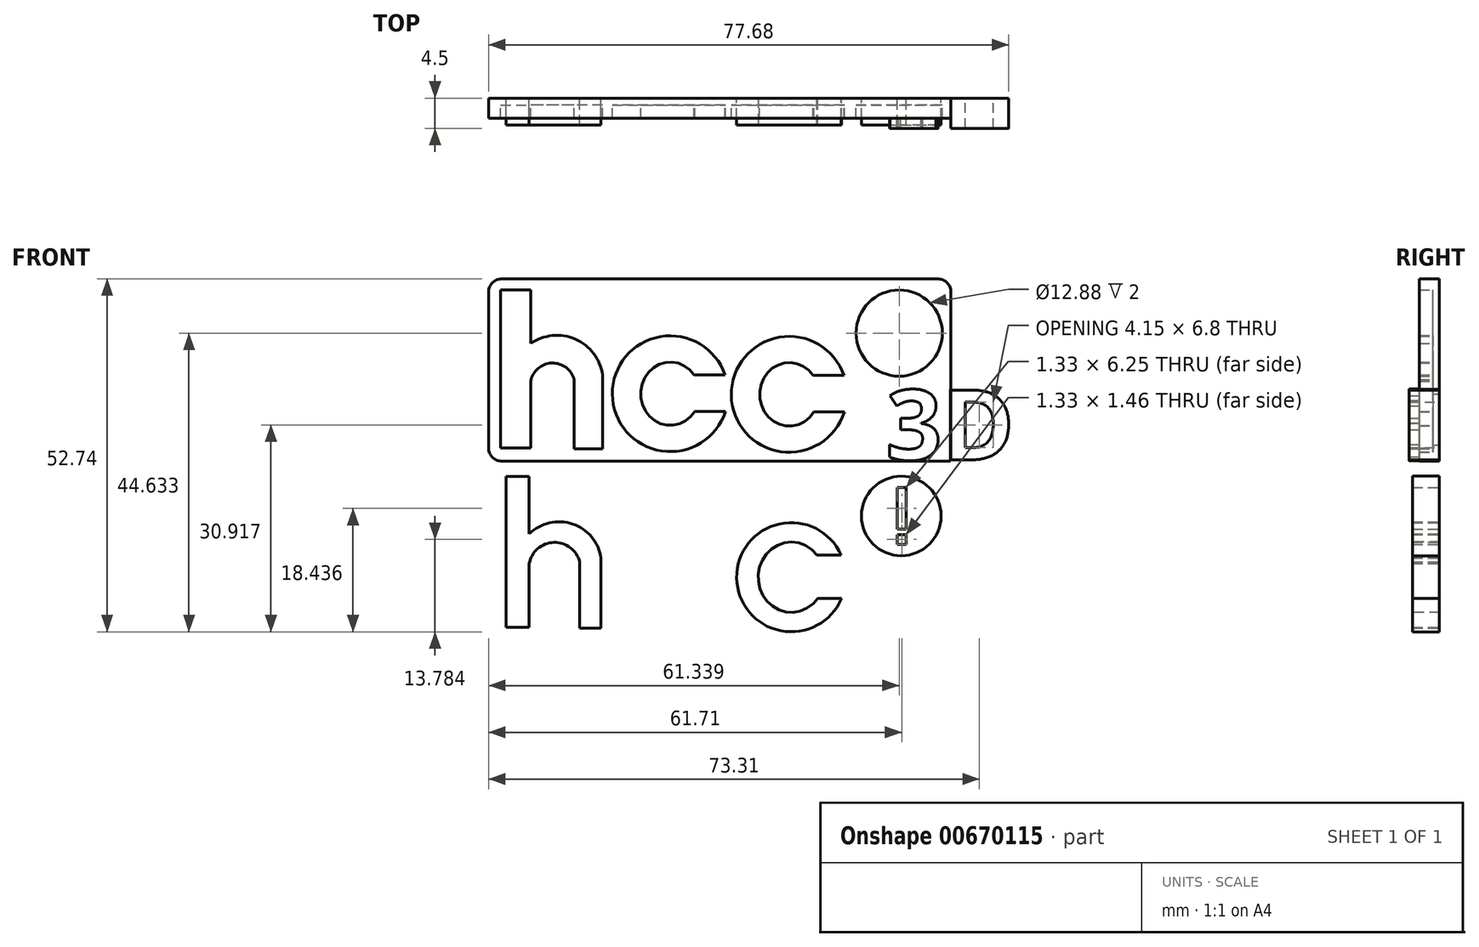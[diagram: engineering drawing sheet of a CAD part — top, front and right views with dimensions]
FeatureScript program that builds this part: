
annotation { "Feature Type Name" : "Feature", "Feature Type Description" : "" }
export const myFeature = defineFeature(function(context is Context, id is Id, definition is map)
    precondition{}
    {
        {
            var Q0;
            Q0=qCreatedBy(makeId("Front.planeOp"),FACE);
            var sketch = newSketch(context, id + "F0", { "sketchPlane" : qUnion([Q0])});
            skLineSegment(sketch, "E0.bottom", {"start": v(32.84, -11.61) * mm, "end": v(-34.55, -11.61) * mm});
            skLineSegment(sketch, "E0.top", {"start": v(32.84, 13.5) * mm, "end": v(-34.55, 13.5) * mm});
            skLineSegment(sketch, "E0.left", {"start": v(32.84, -11.61) * mm, "end": v(32.84, 13.5) * mm});
            skLineSegment(sketch, "E0.right", {"start": v(-34.55, -11.61) * mm, "end": v(-34.55, 13.5) * mm});
            skLineSegment(sketch, "E1.bottom", {"start": v(32.84, -2.93) * mm, "end": v(35.45, -2.93) * mm});
            skLineSegment(sketch, "E1.top", {"start": v(32.84, -10.58) * mm, "end": v(35.45, -10.58) * mm});
            skLineSegment(sketch, "E1.left", {"start": v(32.84, -2.93) * mm, "end": v(32.84, -10.58) * mm});
            skLineSegment(sketch, "E1.right", {"start": v(35.45, -2.93) * mm, "end": v(35.45, -10.58) * mm});
            skSolve(sketch);
        }
        {
            var Q0;
            Q0=qCreatedBy(makeId("Front.planeOp"),FACE);
            var sketch = newSketch(context, id + "F1", { "sketchPlane" : qUnion([Q0])});
            skLineSegment(sketch, "E2.bottom", {"start": v(-29.23, 12.7) * mm, "end": v(-33.71, 12.7) * mm});
            skLineSegment(sketch, "E2.top", {"start": v(-29.23, -10.95) * mm, "end": v(-33.71, -10.95) * mm});
            skLineSegment(sketch, "E2.left", {"start": v(-29.23, 12.7) * mm, "end": v(-29.23, 4.68) * mm});
            skLineSegment(sketch, "E2.right", {"start": v(-33.71, 12.7) * mm, "end": v(-33.71, -10.95) * mm});
            skArc(sketch, "E3", {"start": v(-18.5, 0) * mm, "mid": v(-22.56, 5.32) * mm, "end": v(-29.23, 4.68) * mm});
            skArc(sketch, "E4", {"start": v(-22.75, -0.72) * mm, "mid": v(-26.08, 1.76) * mm, "end": v(-29.23, -0.94) * mm});
            skLineSegment(sketch, "E5", {"start": v(-22.75, -0.72) * mm, "end": v(-22.75, -11.06) * mm});
            skLineSegment(sketch, "E6", {"start": v(-22.75, -11.06) * mm, "end": v(-18.5, -11.06) * mm});
            skLineSegment(sketch, "E7", {"start": v(-18.5, -11.06) * mm, "end": v(-18.5, 0) * mm});
            skArc(sketch, "E8", {"start": v(-0.2, 0) * mm, "mid": v(-17.04, -2.91) * mm, "end": v(-0.14, -5.47) * mm});
            skEllipticalArc(sketch, "E9", {});
            skLineSegment(sketch, "E10", {"start": v(-4.83, 0) * mm, "end": v(0, 0) * mm});
            skLineSegment(sketch, "E11", {"start": v(-4.72, -5.47) * mm, "end": v(0, -5.47) * mm});
            skArc(sketch, "E12", {"start": v(17.56, -0.1) * mm, "mid": v(0.73, -3) * mm, "end": v(17.62, -5.56) * mm});
            skEllipticalArc(sketch, "E13", {});
            skLineSegment(sketch, "E14", {"start": v(12.93, -0.1) * mm, "end": v(17.76, -0.1) * mm});
            skLineSegment(sketch, "E15", {"start": v(13.05, -5.56) * mm, "end": v(17.76, -5.56) * mm});
            skCircle(sketch, "E16", {"center": v(25.8, 6.23) * mm, "radius": 6.44 * mm});
            skLineSegment(sketch, "E17.bottom", {"start": v(25.21, 10.49) * mm, "end": v(26.54, 10.49) * mm});
            skLineSegment(sketch, "E17.top", {"start": v(25.21, 4.24) * mm, "end": v(26.54, 4.24) * mm});
            skLineSegment(sketch, "E17.left", {"start": v(25.21, 10.49) * mm, "end": v(25.21, 4.24) * mm});
            skLineSegment(sketch, "E17.right", {"start": v(26.54, 10.49) * mm, "end": v(26.54, 4.24) * mm});
            skLineSegment(sketch, "E18.bottom", {"start": v(25.21, 3.44) * mm, "end": v(26.54, 3.44) * mm});
            skLineSegment(sketch, "E18.top", {"start": v(25.21, 1.98) * mm, "end": v(26.54, 1.98) * mm});
            skLineSegment(sketch, "E18.left", {"start": v(25.21, 3.44) * mm, "end": v(25.21, 1.98) * mm});
            skLineSegment(sketch, "E18.right", {"start": v(26.54, 3.44) * mm, "end": v(26.54, 1.98) * mm});
            skLineSegment(sketch, "E19.bottom", {"start": v(-35.53, 14.34) * mm, "end": v(33.55, 14.34) * mm});
            skLineSegment(sketch, "E19.top", {"start": v(-35.53, -12.91) * mm, "end": v(33.55, -12.91) * mm});
            skLineSegment(sketch, "E19.left", {"start": v(-35.53, 14.34) * mm, "end": v(-35.53, -12.91) * mm});
            skLineSegment(sketch, "E19.right", {"start": v(33.55, 14.34) * mm, "end": v(33.55, -12.91) * mm});
            skPoint(sketch, "E20.orphan", {"position": v(-32.13, 0) * mm});
            skLineSegment(sketch, "E21.trimOffspring", {"start": v(-29.23, -0.94) * mm, "end": v(-29.23, -10.95) * mm});
            skText(sketch, "E22", { "text": "3D", "fontName": "OpenSans-Bold.ttf"});
            skLineSegment(sketch, "E23.bottom", {"start": v(33.46, -2.18) * mm, "end": v(33.55, -2.18) * mm});
            skLineSegment(sketch, "E23.top", {"start": v(33.46, -2.18) * mm, "end": v(33.55, -2.18) * mm});
            skLineSegment(sketch, "E23.left", {"start": v(33.55, -2.18) * mm, "end": v(33.55, -2.18) * mm});
            skLineSegment(sketch, "E23.right", {"start": v(33.46, -2.18) * mm, "end": v(33.46, -2.18) * mm});
            skLineSegment(sketch, "E24.bottom", {"start": v(33.55, -12.71) * mm, "end": v(33.46, -12.71) * mm});
            skLineSegment(sketch, "E24.top", {"start": v(33.55, -12.91) * mm, "end": v(33.46, -12.91) * mm});
            skLineSegment(sketch, "E24.left", {"start": v(33.46, -12.91) * mm, "end": v(33.46, -12.71) * mm});
            skLineSegment(sketch, "E24.right", {"start": v(33.55, -12.91) * mm, "end": v(33.55, -12.71) * mm});
            skLineSegment(sketch, "E25.bottom", {"start": v(33.64, -12.71) * mm, "end": v(33.46, -12.71) * mm});
            skLineSegment(sketch, "E25.top", {"start": v(33.55, -2.18) * mm, "end": v(33.46, -2.18) * mm});
            skLineSegment(sketch, "E25.left", {"start": v(33.46, -12.71) * mm, "end": v(33.46, -2.18) * mm});
            skLineSegment(sketch, "E26.top", {"start": v(33.46, -2.76) * mm, "end": v(33.55, -2.76) * mm});
            skLineSegment(sketch, "E26.left", {"start": v(33.55, -2.18) * mm, "end": v(33.55, -2.76) * mm});
            skLineSegment(sketch, "E26.right", {"start": v(33.46, -2.18) * mm, "end": v(33.46, -2.76) * mm});
            skLineSegment(sketch, "E27.left", {"start": v(33.55, -3.88) * mm, "end": v(33.55, -12.94) * mm});
            skPoint(sketch, "E28.end.orphan", {"position": v(36.71, 0) * mm});
            skPoint(sketch, "E28.start.orphan", {"position": v(33.55, 0) * mm});
            const initialGuessF1  = {"E9": [-0.00838379468768835, -0.002821371890604496, 0, 1, 0.004734611138701439, 0.0044216665190650265, 5.350779379737523, 4.11952951118792], "E13": [0.009380069561302662, -0.0029154655057936907, 0, 1, 0.004734611138701439, 0.0044216665190650265, 5.350779379737523, 4.11952951118792], "E22": [0.02383, -0.01271, 1, 0, 0.01053]};
            skSetInitialGuess(sketch, initialGuessF1);
            skSolve(sketch);
        }
        {
            var Q0;
            Q0=qSketchRegion(id+"F0",true);
            extrude(context, id + "F2", {"entities" : qUnion([Q0]), "depth" : 1 * mm, "offsetDistance" : 25 * mm});
        }
        {
            var Q0;
            Q0=qCreatedBy(makeId("Front.planeOp"),FACE);
            var sketch = newSketch(context, id + "F3", { "sketchPlane" : qUnion([Q0])});
            skLineSegment(sketch, "E29.bottom", {"start": v(-28.92, -14.64) * mm, "end": v(-33.4, -14.64) * mm});
            skLineSegment(sketch, "E29.top", {"start": v(-28.92, -38.27) * mm, "end": v(-33.4, -38.27) * mm});
            skLineSegment(sketch, "E29.left", {"start": v(-28.92, -14.64) * mm, "end": v(-28.92, -22.65) * mm});
            skLineSegment(sketch, "E29.right", {"start": v(-33.4, -14.64) * mm, "end": v(-33.4, -38.27) * mm});
            skArc(sketch, "E30", {"start": v(-18.2, -27.33) * mm, "mid": v(-22.26, -22) * mm, "end": v(-28.92, -22.65) * mm});
            skArc(sketch, "E31", {"start": v(-22.44, -28.05) * mm, "mid": v(-25.77, -25.57) * mm, "end": v(-28.92, -28.27) * mm});
            skLineSegment(sketch, "E32", {"start": v(-22.44, -28.05) * mm, "end": v(-22.44, -38.39) * mm});
            skLineSegment(sketch, "E33", {"start": v(-22.44, -38.39) * mm, "end": v(-18.2, -38.39) * mm});
            skLineSegment(sketch, "E34", {"start": v(-18.2, -38.39) * mm, "end": v(-18.2, -27.33) * mm});
            skArc(sketch, "E35", {"start": v(0.1, -27.32) * mm, "mid": v(-16.73, -30.25) * mm, "end": v(0.17, -32.77) * mm});
            skEllipticalArc(sketch, "E36", {});
            skLineSegment(sketch, "E37", {"start": v(-4.53, -27.33) * mm, "end": v(0.1, -27.32) * mm});
            skLineSegment(sketch, "E38", {"start": v(-4.4, -32.77) * mm, "end": v(0.16, -32.77) * mm});
            skArc(sketch, "E39", {"start": v(17.87, -27.42) * mm, "mid": v(1.03, -30.33) * mm, "end": v(17.93, -32.89) * mm});
            skEllipticalArc(sketch, "E40", {});
            skLineSegment(sketch, "E41", {"start": v(13.24, -27.42) * mm, "end": v(17.87, -27.42) * mm});
            skLineSegment(sketch, "E42", {"start": v(13.35, -32.89) * mm, "end": v(17.92, -32.89) * mm});
            skCircle(sketch, "E43", {"center": v(26.11, -21.1) * mm, "radius": 6.44 * mm});
            skLineSegment(sketch, "E44.bottom", {"start": v(25.52, -16.84) * mm, "end": v(26.84, -16.84) * mm});
            skLineSegment(sketch, "E44.top", {"start": v(25.52, -23.09) * mm, "end": v(26.84, -23.09) * mm});
            skLineSegment(sketch, "E44.left", {"start": v(25.52, -16.84) * mm, "end": v(25.52, -23.09) * mm});
            skLineSegment(sketch, "E44.right", {"start": v(26.84, -16.84) * mm, "end": v(26.84, -23.09) * mm});
            skLineSegment(sketch, "E45.bottom", {"start": v(25.52, -23.88) * mm, "end": v(26.84, -23.88) * mm});
            skLineSegment(sketch, "E45.top", {"start": v(25.52, -25.35) * mm, "end": v(26.84, -25.35) * mm});
            skLineSegment(sketch, "E45.left", {"start": v(25.52, -23.88) * mm, "end": v(25.52, -25.35) * mm});
            skLineSegment(sketch, "E45.right", {"start": v(26.84, -23.88) * mm, "end": v(26.84, -25.35) * mm});
            skPoint(sketch, "E46.orphan", {"position": v(-31.83, -27.33) * mm});
            skLineSegment(sketch, "E47.trimOffspring", {"start": v(-28.92, -28.27) * mm, "end": v(-28.92, -38.27) * mm});
            skLineSegment(sketch, "E48.0", {"start": v(-29.45, -15.16) * mm, "end": v(-29.45, -23.76) * mm});
            skArc(sketch, "E48.1", {"start": v(-18.72, -27.37) * mm, "mid": v(-22.99, -22.29) * mm, "end": v(-29.45, -23.76) * mm});
            skLineSegment(sketch, "E48.2", {"start": v(-29.45, -15.16) * mm, "end": v(-32.88, -15.16) * mm});
            skLineSegment(sketch, "E48.3", {"start": v(-18.72, -37.86) * mm, "end": v(-18.72, -27.37) * mm});
            skLineSegment(sketch, "E48.4", {"start": v(-21.91, -37.86) * mm, "end": v(-18.72, -37.86) * mm});
            skLineSegment(sketch, "E48.5", {"start": v(-21.91, -27.98) * mm, "end": v(-21.91, -37.86) * mm});
            skLineSegment(sketch, "E48.6", {"start": v(-32.88, -15.16) * mm, "end": v(-32.88, -37.75) * mm});
            skLineSegment(sketch, "E48.7", {"start": v(-29.45, -37.75) * mm, "end": v(-32.88, -37.75) * mm});
            skLineSegment(sketch, "E48.8", {"start": v(-29.45, -28.22) * mm, "end": v(-29.45, -37.75) * mm});
            skArc(sketch, "E48.9", {"start": v(-21.91, -27.98) * mm, "mid": v(-25.78, -25.04) * mm, "end": v(-29.45, -28.22) * mm});
            skCircle(sketch, "E49.0", {"center": v(26.11, -21.1) * mm, "radius": 5.94 * mm});
            skArc(sketch, "E50.0", {"start": v(-0.63, -26.82) * mm, "mid": v(-16.23, -30.26) * mm, "end": v(-0.55, -33.27) * mm});
            skLineSegment(sketch, "E50.1", {"start": v(-4.27, -26.83) * mm, "end": v(-0.63, -26.82) * mm});
            skFitSpline(sketch, "E50.2", {"points": [v(-7.1, -24.98) * mm, v(-8.08, -24.88) * mm, v(-9.05, -24.98) * mm, v(-9.98, -25.28) * mm, v(-10.85, -25.78) * mm, v(-11.6, -26.44) * mm, v(-12.2, -27.23) * mm, v(-12.66, -28.15) * mm, v(-12.94, -29.12) * mm, v(-13.03, -30.15) * mm, v(-12.94, -31.17) * mm, v(-12.66, -32.15) * mm, v(-12.2, -33.06) * mm, v(-11.6, -33.86) * mm, v(-10.85, -34.52) * mm, v(-9.98, -35.01) * mm, v(-9.05, -35.31) * mm, v(-8.08, -35.42) * mm, v(-7.1, -35.31) * mm, v(-6.17, -35.01) * mm, v(-5.31, -34.52) * mm, v(-4.56, -33.86) * mm, v(-3.95, -33.06) * mm, v(-3.5, -32.15) * mm, v(-3.22, -31.17) * mm, v(-3.13, -30.15) * mm, v(-3.22, -29.12) * mm, v(-3.5, -28.15) * mm, v(-3.95, -27.23) * mm, v(-4.56, -26.44) * mm, v(-5.31, -25.78) * mm, v(-6.17, -25.28) * mm, v(-7.1, -24.98) * mm, v(-8.08, -24.88) * mm, v(-9.05, -24.98) * mm]});
            skLineSegment(sketch, "E50.3", {"start": v(-4.13, -33.27) * mm, "end": v(-0.55, -33.27) * mm});
            skArc(sketch, "E51.0", {"start": v(17.13, -26.92) * mm, "mid": v(1.53, -30.34) * mm, "end": v(17.2, -33.39) * mm});
            skLineSegment(sketch, "E51.1", {"start": v(13.49, -26.92) * mm, "end": v(17.13, -26.92) * mm});
            skFitSpline(sketch, "E51.2", {"points": [v(13.65, -27.14) * mm, v(13.34, -26.7) * mm, v(12.78, -26.1) * mm, v(11.89, -25.53) * mm, v(11.16, -25.23) * mm, v(10.4, -25.04) * mm, v(9.6, -24.99) * mm, v(8.83, -25.06) * mm, v(8.07, -25.27) * mm, v(7.35, -25.6) * mm, v(6.7, -26.05) * mm, v(6.11, -26.6) * mm, v(5.62, -27.25) * mm, v(5.23, -27.96) * mm, v(4.95, -28.73) * mm, v(4.79, -29.54) * mm, v(4.74, -30.36) * mm, v(4.82, -31.18) * mm, v(5.02, -31.97) * mm, v(5.33, -32.73) * mm, v(5.75, -33.43) * mm, v(6.27, -34.04) * mm, v(6.88, -34.57) * mm, v(7.55, -34.98) * mm, v(8.28, -35.28) * mm, v(9.05, -35.46) * mm, v(9.83, -35.5) * mm, v(10.62, -35.4) * mm, v(11.37, -35.18) * mm, v(12.08, -34.84) * mm, v(12.95, -34.22) * mm, v(13.49, -33.61) * mm, v(13.77, -33.16) * mm]});
            skLineSegment(sketch, "E51.3", {"start": v(13.62, -33.39) * mm, "end": v(17.2, -33.39) * mm});
            const initialGuessF3  = {"E36": [-0.008079084567725658, -0.030148023739457127, 0, 1, 0.004734611138701439, 0.0044216665190650265, 5.350779407726535, 4.125229414550572], "E40": [0.009684779681265354, -0.03024211735464632, 0, 1, 0.004734611138701439, 0.0044216665190650265, 5.350779379737523, 4.11915715223877]};
            skSetInitialGuess(sketch, initialGuessF3);
            skSolve(sketch);
        }
        {
            var Q0;
            Q0=makeQuery(id+"F1.imprint","IMPRINT",FACE,{"disambiguationData":[TD([[makeQuery(id+"F1.imprint","IMPRINT",EDGE,{"derivedFrom":sQuery(id+"F1.wireOp",EDGE,"E22.sketch_text.stroke-27")}),-1.0]])]});
            var Q1;
            Q1=makeQuery(id+"F1.imprint","IMPRINT",FACE,{"disambiguationData":[TD([[makeQuery(id+"F1.imprint","IMPRINT",EDGE,{"derivedFrom":sQuery(id+"F1.wireOp",EDGE,"E22.sketch_text.stroke-0")}),-1.0]])]});
            extrude(context, id + "F4", {"entities" : qUnion([Q0, Q1]), "operationType" : NewBodyOperationType.ADD, "depth" : 4.5 * mm, "offsetDistance" : 25 * mm});
        }
        {
            var Q0;
            Q0=makeQuery(id+"F1.imprint","IMPRINT",FACE,{"disambiguationData":[TD([[makeQuery(id+"F1.imprint","IMPRINT",EDGE,{"derivedFrom":sQuery(id+"F1.wireOp",EDGE,"E22.sketch_text.stroke-27")}),-1.0]])]});
            var Q1;
            Q1=makeQuery(id+"F1.imprint","IMPRINT",FACE,{"disambiguationData":[TD([[makeQuery(id+"F1.imprint","IMPRINT",EDGE,{"derivedFrom":sQuery(id+"F1.wireOp",EDGE,"E2.bottom")}),-1.0]])]});
            extrude(context, id + "F5", {"entities" : qUnion([Q0, Q1]), "operationType" : NewBodyOperationType.ADD, "depth" : 3 * mm, "offsetDistance" : 25 * mm});
        }
        {
            var Q0;
            Q0=makeQuery(id+"F5.opExtrude","SWEPT_EDGE",EDGE,{"disambiguationData":[OSD([sQuery(id+"F1.wireOp",EDGE,"E19.bottom"),sQuery(id+"F1.wireOp",EDGE,"E19.left")])]});
            var Q1;
            Q1=makeQuery(id+"F5.opExtrude","SWEPT_EDGE",EDGE,{"disambiguationData":[OSD([sQuery(id+"F1.wireOp",EDGE,"E19.top"),sQuery(id+"F1.wireOp",EDGE,"E19.left")])]});
            var Q2;
            Q2=makeQuery(id+"F5.opExtrude","SWEPT_EDGE",EDGE,{"disambiguationData":[OSD([sQuery(id+"F1.wireOp",EDGE,"E19.bottom"),sQuery(id+"F1.wireOp",EDGE,"E19.right")])]});
            fillet(context, id + "F6", {"entities" : qUnion([Q0, Q1, Q2]), "radius" : 2 * mm, "tangentPropagation" : true, "allowEdgeOverflow" : false});
        }
        {
            var Q0;
            Q0=makeQuery(id+"F3.imprint","IMPRINT",FACE,{"disambiguationData":[TD([[makeQuery(id+"F3.imprint","IMPRINT",EDGE,{"derivedFrom":sQuery(id+"F3.wireOp",EDGE,"E48.0")}),-1.0]])]});
            var Q1;
            Q1=makeQuery(id+"F3.imprint","IMPRINT",FACE,{"disambiguationData":[TD([[makeQuery(id+"F3.imprint","IMPRINT",EDGE,{"derivedFrom":sQuery(id+"F3.wireOp",EDGE,"E50.0")}),1.0]])]});
            var Q2;
            Q2=makeQuery(id+"F3.imprint","IMPRINT",FACE,{"disambiguationData":[TD([[makeQuery(id+"F3.imprint","IMPRINT",EDGE,{"derivedFrom":sQuery(id+"F3.wireOp",EDGE,"E51.0")}),1.0]])]});
            var Q3;
            Q3=makeQuery(id+"F3.imprint","IMPRINT",FACE,{"disambiguationData":[TD([[makeQuery(id+"F3.imprint","IMPRINT",EDGE,{"derivedFrom":sQuery(id+"F3.wireOp",EDGE,"E44.bottom")}),1.0]])]});
            extrude(context, id + "F7", {"entities" : qUnion([Q0, Q1, Q2, Q3]), "depth" : 4 * mm, "offsetDistance" : 25 * mm});
        }
    });
